# Revit family: Toilet_Seat-Elongated_Closed_Front-KOHLER-FREELANCE-K-4735IN_1
name_source: partatom
category: Specialty Equipment
revit_build: Autodesk Revit 2017 (Build: 20160225_1515(x64)
units: mm (PartAtom-declared; Revit-internal decimal feet)

## family parameters
Cut with Voids When Loaded = No
Host = Face
OmniClass Number = 23.31.25.00
OmniClass Title = Toilet and Bath Specialties
Part Type = Normal
Room Calculation Point = No
Round Connector Dimension = Use Diameter
Shared = No

## types (5) — shared parameters
ADA Compliant = No
Assembly Code = C1030200
Date Modified = 12/23/2020
Default Elevation = 0"
Height = 2 13/16"
Length = 17 11/16"
Manufacturer = KOHLER Co.
Master Format 2014 = 10 28 00
Master Format 2014 Name = Toilet, Bath, and Laundry Accessories
Material = Plastic
Product Name = FREELANCE
URL = https://www.kohler.co.in
WaterSense Certified = No
Width = 15 1/8"

## per-type parameters (varying)
| type | Description | Finish | Model | Product Page URL | Type |
| 0-White | QUIET CLOSE TOILET SEAT | Kohler-Plastic-0-White | K-4735IN-0 |  | 1 |
| 96- Biscuit | QUIET CLOSE TOILET SEAT | Kohler-Plastic-96-Biscuit | K-4735IN-96 |  | 2 |
| UF,0- White | Toilet Seat with Cover | Kohler-Plastic-0-White | K-4735IN-UF-0 | https://www.kohler.co.in | 3 |
| PP,0- White | Toilet Seat with Cover | Kohler-Plastic-0-White | K-4735IN-PP-0 |  | 4 |
| PP,96- Biscuit | Toilet Seat with Cover | Kohler-Plastic-96-Biscuit | K-4735IN-PP-96 |  | 5 |

## geometry (parser evidence)
native form markers: Sweep x4
no freeform markers — native parametric forms only
